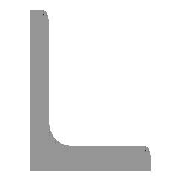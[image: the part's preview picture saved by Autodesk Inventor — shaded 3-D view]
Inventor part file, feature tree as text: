
AUTODESK INVENTOR PART (.ipt)
format: ipt  version: 2013 (Build 170138000, 138)  size: 149,504 bytes
history: native  units: mm (DEFAULTED — no unit token found)
features: plane x7, other x4, sketch x4, extrude x2
ambient origin geometry x8: Origin, YZ Plane, XZ Plane, XY Plane, X Axis, Y Axis, Z Axis, Center Point
bodies: Solid1 (feature_tree), Body (feature_tree)
feature tree (17):
  parser-record x1  (decoder bookkeeping rows leaked as tree rows — omitted from the tree; the rows remain in map.json)
  other  "Driven Length"
  other  "Start plane"
  other  "End plane"
  plane  "Work Plane4"
  plane  "Work Plane5"
  plane  "Work Plane6"
  extrude  "Extrusion2"  Depth=38.1mm
  plane  "Work Plane7"
  plane  "Work Plane8"
  plane  "Work Plane9"
  extrude  "Extrusion3"  Depth=4.7625mm
  sketch  "Sketch3"  dims[d0=38.1mm d1=38.1mm]
  plane  "Work Plane3"
  sketch  "Sketch4"  dims[d2=4.7625mm d3=4.7625mm]
  sketch  "Sketch5"  dims[d4=558.8mm]
  sketch  "Sketch6"  dims[d5=0.0mm d10=0.0mm d11=0.0mm d12=-0.0mm d13=558.8mm d14=4.826mm d15=2.286mm d16=90.0deg d17=558.8mm d18=3.302mm d19=0.0mm d20=3.302mm d21=0.0mm]
